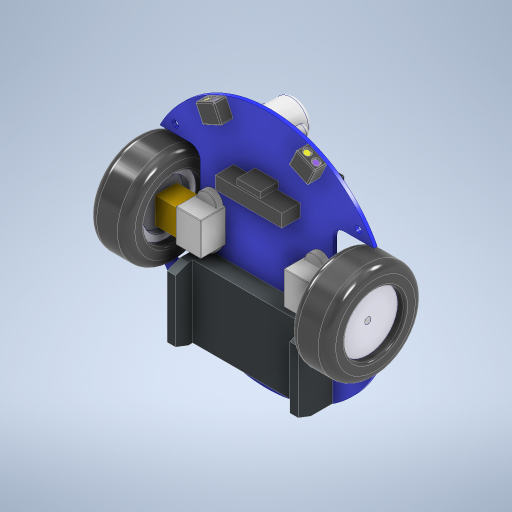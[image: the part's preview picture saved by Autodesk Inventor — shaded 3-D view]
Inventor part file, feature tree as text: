
AUTODESK INVENTOR PART (.ipt)
format: ipt  version: 2023 (Build 270158000, 158)  size: 1,063,424 bytes
history: native  units: mm
features: extrude x22, other x16, sketch x15, projected_geometry x12, fillet x11, mirror x7, plane x2, revolve x1, pattern_linear x1
ambient origin geometry x8: Origin, YZ Plane, XZ Plane, XY Plane, X Axis, Y Axis, Z Axis, Center Point
bodies: Body1 (feature_tree), Body2 (feature_tree), Body3 (feature_tree), Body4 (feature_tree), Body5 (feature_tree), Body6 (feature_tree), Body7 (feature_tree), Body8 (feature_tree), Body9 (feature_tree), Body10 (feature_tree), Body11 (feature_tree), Body12 (feature_tree), Body13 (feature_tree), Body14 (feature_tree), Body15 (feature_tree), Body16 (feature_tree), Body17 (feature_tree)
feature tree (87):
  other  "Sólido1"
  extrude  "Extrusión1"  Depth=50.0mm
  fillet  "Empalme1"  Radius=18.5mm
  sketch  "Boceto2"  dims[d3=18.5mm d4=1.6mm d5=0.0mm]
  extrude  "Extrusión2"  Depth=1.6mm TaperAngle=0.0deg
  extrude  "Extrusión3"  Depth=5.0mm
  fillet  "Empalme2"  Radius=5.5mm
  plane  "Plano de trabajo1"
  revolve  "Revolución1"  [1 undecoded]
  mirror  "Simetría1"
  sketch  "Boceto5"  dims[d9=11.5mm d10=0.0mm d11=8.0mm d12=0.0mm]
  extrude  "Extrusión4"  Depth=2.0mm
  extrude  "Extrusión5"  TaperAngle=90.0deg  [1 undecoded]
  pattern_linear  "Patrón rectangular1"  Count1=3 Spacing1=12.5mm
  fillet  "Empalme3"  Radius=30.0mm
  sketch  "Boceto6"  dims[d13=2.0mm d14=9.0mm]
  extrude  "Extrusión6"  Depth=8.35mm
  extrude  "Extrusión7"  Depth=8.35mm
  fillet  "Empalme4"  Radius=2.9mm
  mirror  "Simetría2"
  sketch  "Boceto7"  dims[d15=10.5mm d16=90.0deg]
  extrude  "Extrusión8"  Depth=2.75mm
  fillet  "Empalme5"  Radius=5.1mm
  extrude  "Extrusión9"  Depth=8.35mm TaperAngle=0.0deg
  fillet  "Empalme6"  Radius=0.2mm
  sketch  "Boceto8"  dims[d17=5.0mm]
  extrude  "Extrusión10"  Depth=4.0mm
  extrude  "Extrusión11"  Depth=5.0mm
  sketch  "Boceto9"  dims[d18=6.6mm]
  extrude  "Extrusión12"  Depth=8.35mm
  mirror  "Simetría3"
  mirror  "Simetría4"
  extrude  "Extrusión13"  Depth=8.35mm
  fillet  "Empalme7"  Radius=3.0mm
  extrude  "Extrusión14"  Depth=8.35mm
  fillet  "Empalme8"  Radius=5.0mm
  mirror  "Simetría6"
  extrude  "Extrusión15"  Depth=8.35mm
  extrude  "Extrusión16"  Depth=8.35mm
  sketch  "Boceto14"  dims[d23=6.55mm d24=0.0mm]
  extrude  "Extrusión17"  Depth=8.35mm
  extrude  "Extrusión18"  Depth=3.0mm
  extrude  "Extrusión19"  Depth=8.35mm
  fillet  "Empalme9"  Radius=2.6mm
  fillet  "Empalme10"  Radius=1.2mm
  fillet  "Empalme11"  Radius=16.0mm
  mirror  "Simetría7"
  sketch  "Boceto15"  dims[d25=6.25mm d26=0.0mm d27=30.0mm d29=12.5mm d30=30.0mm d32=12.5mm]
  extrude  "Extrusión20"  Depth=1.25mm TaperAngle=0.0deg
  extrude  "Extrusión21"  Depth=0.2mm
  mirror  "Simetría8"
  extrude  "Extrusión22"  Depth=1.5mm TaperAngle=0.0deg
  sketch  "Boceto1"  dims[d0=110.0mm d1=50.0mm d2=18.5mm]
  other  "Sólido2"
  other  "Sólido3"
  sketch  "Boceto4"  dims[d6=5.0mm d7=15.75mm d8=5.5mm]
  projected_geometry  "Contorno proyectado1"
  other  "Sólido4"
  projected_geometry  "Contorno proyectado2"
  other  "IR_S1"
  projected_geometry  "Contorno proyectado3"
  other  "Sólido6"
  projected_geometry  "Contorno proyectado4"
  other  "Sólido7"
  other  "Sólido8"
  projected_geometry  "Contorno proyectado5"
  other  "Sólido9"
  other  "Sólido10"
  projected_geometry  "Contorno proyectado6"
  sketch  "Boceto10"  dims[d19=2.25mm]
  projected_geometry  "Contorno proyectado7"
  sketch  "Boceto11"  dims[d20=1.65mm]
  sketch  "Boceto12"  dims[d21=1.65mm]
  projected_geometry  "Contorno proyectado8"
  other  "Sólido12"
  sketch  "Boceto13"  dims[d22=32.5mm]
  projected_geometry  "Contorno proyectado9"
  other  "Sólido13"
  projected_geometry  "Contorno proyectado10"
  other  "Sólido14"
  other  "Sólido15"
  projected_geometry  "Contorno proyectado11"
  other  "Sólido16"
  sketch  "Boceto16"  dims[d33=0.2mm d34=6.9mm d35=4.5mm d36=2.9mm d37=2.75mm d38=5.1mm d39=0.0mm d40=4.9mm d41=0.0mm d42=0.2mm d43=4.0mm d44=5.0mm d45=3.15mm d46=12.5mm d47=3.0mm d48=12.5mm d49=5.0mm d50=7.15mm d51=6.5mm d52=11.25mm d53=3.0mm d54=6.0mm d55=2.6mm d56=1.2mm d57=16.0mm d58=1.25mm d59=0.0mm d60=0.2mm d61=1.5mm d62=0.0mm d63=0.2mm d64=11.5mm d65=15.25mm d66=9.25mm d67=15.0mm d68=11.25mm d69=0.0mm d70=3.0mm d71=0.0mm d72=12.0mm d73=9.95mm d74=3.0mm d75=26.04mm d76=41.91mm d77=10.0mm d78=0.0mm d79=4.363323mm d80=9.55mm d81=8.25mm d82=5.5mm d83=0.0mm d84=0.5mm d85=3.0mm d86=2.25mm d87=2.25mm d88=0.5mm d89=0.0mm d90=0.25mm d91=10.75mm d92=0.0mm d93=2.9mm d94=10.0mm d95=0.0mm d96=8.5mm d97=27.5mm d98=21.5mm d99=10.0mm d100=0.0mm d101=7.0mm d102=0.0mm d103=3.5mm d104=14.0mm d105=0.0mm d106=0.0mm d107=4.0mm d108=1.0mm d109=0.25mm d110=5.85mm d111=30.5mm d112=32.85mm d113=60.0mm d114=7.85mm d115=0.0mm d116=28.35mm d117=7.84mm d118=2.0mm d119=3.85mm d120=0.0mm d121=33.6mm d122=10.75mm d123=2.6mm d124=1.0mm d125=8.35mm d126=0.0mm]
  projected_geometry  "Contorno proyectado12"
  plane  "Plano de trabajo2"
  other  "Sólido17"
note: 2 required parameter values undecoded (feature->parameter linkage not recoverable at this tier; creation-order binding heuristic only, values carry confidence <= 0.55)